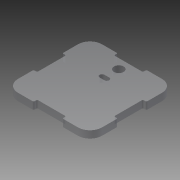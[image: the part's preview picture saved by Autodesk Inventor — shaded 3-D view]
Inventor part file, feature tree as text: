
AUTODESK INVENTOR PART (.ipt)
format: ipt  version: 2015 (Build 190159000, 159)  size: 159,744 bytes
history: native  units: mm
features: extrude x2, sketch x2
ambient origin geometry x8: Origin, YZ Plane, XZ Plane, XY Plane, X Axis, Y Axis, Z Axis, Center Point
bodies: Body1 (feature_tree)
feature tree (4):
  extrude  "Extrusion6"  Depth=4.0mm
  extrude  "Extrusion8"  Depth=10.0mm
  sketch  "Sketch1"  dims[d0=31.75mm d6=4.0mm]
  sketch  "Sketch4"  dims[d11=10.0mm d12=5.0mm d15=36.0mm d19=18.0mm d20=18.0mm d44=12.0mm d45=0.5mm d46=40.0mm d48=360.0deg d50=5.0mm d62=3.0mm d63=0.0mm d64=12.0mm d65=16.0mm d66=35.0mm d76=2.0mm d77=4.0mm d78=5.0mm d79=1.0mm d80=10.0mm d81=0.0mm]
